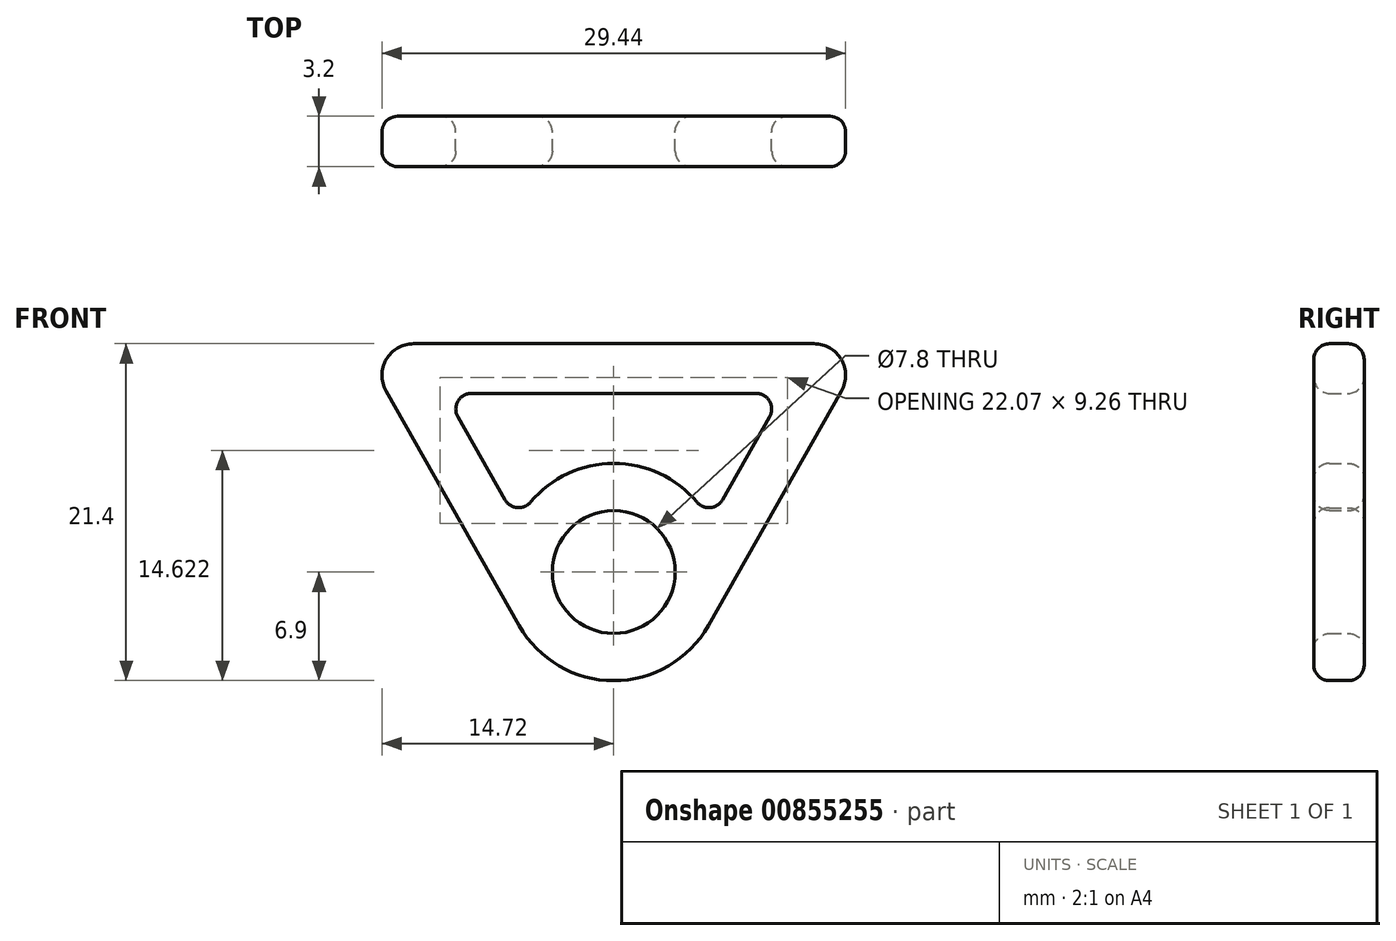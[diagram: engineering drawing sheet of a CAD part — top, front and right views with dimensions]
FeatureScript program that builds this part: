
annotation { "Feature Type Name" : "Feature", "Feature Type Description" : "" }
export const myFeature = defineFeature(function(context is Context, id is Id, definition is map)
    precondition{}
    {
        {
            var Q0;
            Q0=qCreatedBy(makeId("Front.planeOp"),FACE);
            var sketch = newSketch(context, id + "F0", { "sketchPlane" : qUnion([Q0])});
            skArc(sketch, "E0", {"start": v(-6, -3.4) * mm, "mid": v(0, -6.9) * mm, "end": v(6, -3.4) * mm});
            skCircle(sketch, "E1", {"center": v(0, 0) * mm, "radius": 3.9 * mm});
            skLineSegment(sketch, "E2", {"start": v(-9.03, 11.35) * mm, "end": v(9.03, 11.35) * mm});
            skLineSegment(sketch, "E3", {"start": v(9.9, 9.86) * mm, "end": v(6.92, 4.6) * mm});
            skLineSegment(sketch, "E4", {"start": v(-9.9, 9.86) * mm, "end": v(-6.92, 4.6) * mm});
            skLineSegment(sketch, "E5", {"start": v(-12.72, 14.5) * mm, "end": v(12.72, 14.5) * mm});
            skLineSegment(sketch, "E6", {"start": v(14.46, 11.51) * mm, "end": v(6, -3.4) * mm});
            skLineSegment(sketch, "E7", {"start": v(-14.46, 11.51) * mm, "end": v(-6, -3.4) * mm});
            skLineSegment(sketch, "E8", {"start": v(0, 0) * mm, "end": v(0, 11.35) * mm, "construction": true});
            skLineSegment(sketch, "E9", {"start": v(-15.7, -6.9) * mm, "end": v(8.13, -6.9) * mm, "construction": true});
            skPoint(sketch, "E10.visualSharp", {"position": v(-16.16, 14.5) * mm});
            skArc(sketch, "E10.filletArc", {"start": v(-12.72, 14.5) * mm, "mid": v(-14.45, 13.5) * mm, "end": v(-14.46, 11.51) * mm});
            skPoint(sketch, "E11.visualSharp", {"position": v(16.16, 14.5) * mm});
            skArc(sketch, "E11.filletArc", {"start": v(14.46, 11.51) * mm, "mid": v(14.45, 13.5) * mm, "end": v(12.72, 14.5) * mm});
            skArc(sketch, "E12.trimOffspring", {"start": v(5.28, 4.44) * mm, "mid": v(0, 6.9) * mm, "end": v(-5.28, 4.44) * mm});
            skPoint(sketch, "E13.visualSharp", {"position": v(-10.75, 11.35) * mm});
            skArc(sketch, "E13.filletArc", {"start": v(-9.03, 11.35) * mm, "mid": v(-9.9, 10.85) * mm, "end": v(-9.9, 9.86) * mm});
            skPoint(sketch, "E14.visualSharp", {"position": v(10.75, 11.35) * mm});
            skArc(sketch, "E14.filletArc", {"start": v(9.9, 9.86) * mm, "mid": v(9.9, 10.85) * mm, "end": v(9.03, 11.35) * mm});
            skPoint(sketch, "E15.visualSharp", {"position": v(6.12, 3.19) * mm});
            skArc(sketch, "E15.filletArc", {"start": v(5.28, 4.44) * mm, "mid": v(6.14, 4.09) * mm, "end": v(6.92, 4.6) * mm});
            skPoint(sketch, "E16.visualSharp", {"position": v(-6.12, 3.19) * mm});
            skArc(sketch, "E16.filletArc", {"start": v(-6.92, 4.6) * mm, "mid": v(-6.14, 4.09) * mm, "end": v(-5.28, 4.44) * mm});
            skSolve(sketch);
        }
        {
            var Q0;
            Q0=makeQuery(id+"F0.imprint","IMPRINT",FACE,{"disambiguationData":[TD([[makeQuery(id+"F0.imprint","IMPRINT",EDGE,{"derivedFrom":sQuery(id+"F0.wireOp",EDGE,"E0")}),1.0]])]});
            extrude(context, id + "F1", {"entities" : qUnion([Q0]), "depth" : 3.2 * mm, "offsetDistance" : 25 * mm});
        }
        {
            var Q0;
            Q0=makeQuery(id+"F1.opExtrude","CAP_FACE",FACE,{"disambiguationData":[OSD([sQuery(id+"F0.wireOp",EDGE,"E0"),sQuery(id+"F0.wireOp",EDGE,"E1"),sQuery(id+"F0.wireOp",EDGE,"E2"),sQuery(id+"F0.wireOp",EDGE,"E3"),sQuery(id+"F0.wireOp",EDGE,"E4"),sQuery(id+"F0.wireOp",EDGE,"E5"),sQuery(id+"F0.wireOp",EDGE,"E6"),sQuery(id+"F0.wireOp",EDGE,"E7"),sQuery(id+"F0.wireOp",EDGE,"E10.filletArc"),sQuery(id+"F0.wireOp",EDGE,"E11.filletArc"),sQuery(id+"F0.wireOp",EDGE,"E12.trimOffspring"),sQuery(id+"F0.wireOp",EDGE,"E13.filletArc"),sQuery(id+"F0.wireOp",EDGE,"E14.filletArc"),sQuery(id+"F0.wireOp",EDGE,"E15.filletArc"),sQuery(id+"F0.wireOp",EDGE,"E16.filletArc")])],"isStart":false});
            var Q1;
            Q1=makeQuery(id+"F1.opExtrude","CAP_FACE",FACE,{"disambiguationData":[OSD([sQuery(id+"F0.wireOp",EDGE,"E0"),sQuery(id+"F0.wireOp",EDGE,"E1"),sQuery(id+"F0.wireOp",EDGE,"E2"),sQuery(id+"F0.wireOp",EDGE,"E3"),sQuery(id+"F0.wireOp",EDGE,"E4"),sQuery(id+"F0.wireOp",EDGE,"E5"),sQuery(id+"F0.wireOp",EDGE,"E6"),sQuery(id+"F0.wireOp",EDGE,"E7"),sQuery(id+"F0.wireOp",EDGE,"E10.filletArc"),sQuery(id+"F0.wireOp",EDGE,"E11.filletArc"),sQuery(id+"F0.wireOp",EDGE,"E12.trimOffspring"),sQuery(id+"F0.wireOp",EDGE,"E13.filletArc"),sQuery(id+"F0.wireOp",EDGE,"E14.filletArc"),sQuery(id+"F0.wireOp",EDGE,"E15.filletArc"),sQuery(id+"F0.wireOp",EDGE,"E16.filletArc")])],"isStart":true});
            fillet(context, id + "F2", {"entities" : qUnion([Q0, Q1]), "radius" : 1 * mm, "tangentPropagation" : true, "allowEdgeOverflow" : false});
        }
    });
